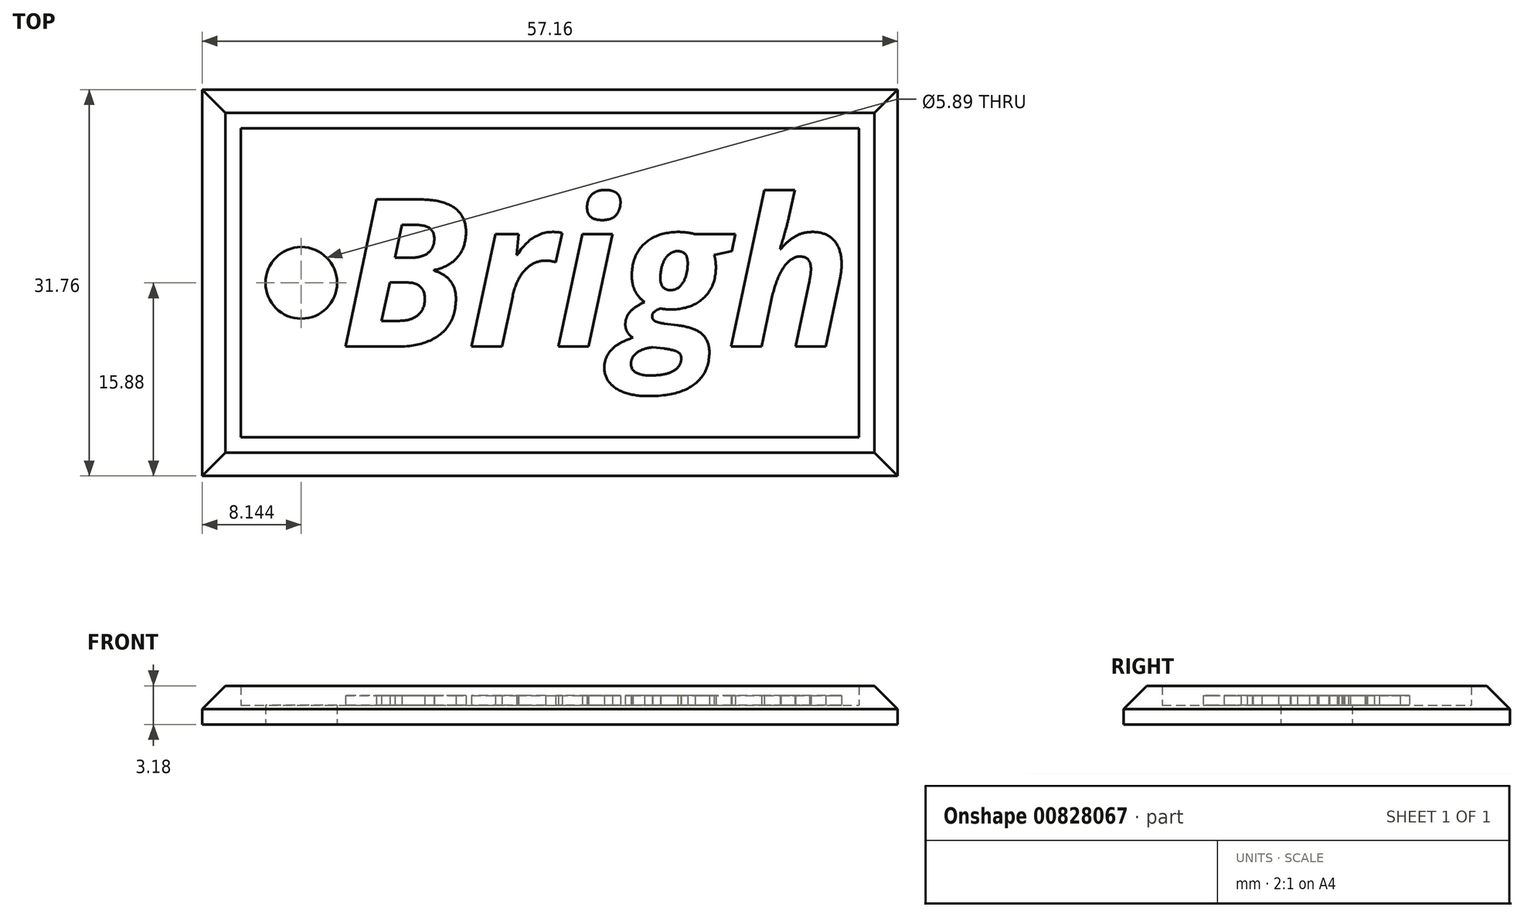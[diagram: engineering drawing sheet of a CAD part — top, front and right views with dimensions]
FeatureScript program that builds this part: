
annotation { "Feature Type Name" : "Feature", "Feature Type Description" : "" }
export const myFeature = defineFeature(function(context is Context, id is Id, definition is map)
    precondition{}
    {
        {
            var Q0;
            Q0=qCreatedBy(makeId("Top.planeOp"),FACE);
            var sketch = newSketch(context, id + "F0", { "sketchPlane" : qUnion([Q0])});
            skLineSegment(sketch, "E0.bottom", {"start": v(0, 0) * mm, "end": v(50.8, 0) * mm});
            skLineSegment(sketch, "E0.top", {"start": v(0, 25.4) * mm, "end": v(50.8, 25.4) * mm});
            skLineSegment(sketch, "E0.left", {"start": v(0, 0) * mm, "end": v(0, 25.4) * mm});
            skLineSegment(sketch, "E0.right", {"start": v(50.8, 0) * mm, "end": v(50.8, 25.4) * mm});
            skCircle(sketch, "E1", {"center": v(4.96, 12.7) * mm, "radius": 2.95 * mm});
            skLineSegment(sketch, "E2.0", {"start": v(-3.18, 28.58) * mm, "end": v(53.98, 28.58) * mm});
            skLineSegment(sketch, "E2.1", {"start": v(-3.18, -3.18) * mm, "end": v(-3.18, 28.58) * mm});
            skLineSegment(sketch, "E2.2", {"start": v(-3.18, -3.18) * mm, "end": v(53.98, -3.18) * mm});
            skLineSegment(sketch, "E2.3", {"start": v(53.98, -3.18) * mm, "end": v(53.98, 28.58) * mm});
            skSolve(sketch);
        }
        {
            var Q0;
            Q0=makeQuery(id+"F0.imprint","IMPRINT",FACE,{"disambiguationData":[TD([[makeQuery(id+"F0.imprint","IMPRINT",EDGE,{"derivedFrom":sQuery(id+"F0.wireOp",EDGE,"E0.bottom")}),1.0]])]});
            extrude(context, id + "F1", {"entities" : qUnion([Q0]), "depth" : 1.59 * mm, "offsetDistance" : 25.4 * mm});
        }
        {
            var Q0;
            Q0 = qSketchRegion(id + "F0", true);
            extrude(context, id + "F2", {"entities" : qUnion([Q0]), "operationType" : NewBodyOperationType.ADD, "depth" : 3.17 * mm, "offsetDistance" : 25.4 * mm});
        }
        {
            var Q0;
            Q0=makeQuery(id+"F2.opExtrude","CAP_EDGE",EDGE,{"disambiguationData":[OSD([sQuery(id+"F0.wireOp",EDGE,"E2.2")])],"isStart":false});
            var Q1;
            Q1=makeQuery(id+"F2.opExtrude","CAP_EDGE",EDGE,{"disambiguationData":[OSD([sQuery(id+"F0.wireOp",EDGE,"E2.1")])],"isStart":false});
            var Q2;
            Q2=makeQuery(id+"F2.opExtrude","CAP_EDGE",EDGE,{"disambiguationData":[OSD([sQuery(id+"F0.wireOp",EDGE,"E2.0")])],"isStart":false});
            var Q3;
            Q3=makeQuery(id+"F2.opExtrude","CAP_EDGE",EDGE,{"disambiguationData":[OSD([sQuery(id+"F0.wireOp",EDGE,"E2.3")])],"isStart":false});
            chamfer(context, id + "F3", {"entities" : qUnion([Q0, Q1, Q2, Q3]), "width" : 1.9 * mm, "tangentPropagation" : true});
        }
        {
            var Q0;
            Q0=makeQuery(id+"F1.opExtrude","CAP_FACE",FACE,{"disambiguationData":[OSD([sQuery(id+"F0.wireOp",EDGE,"E0.bottom"),sQuery(id+"F0.wireOp",EDGE,"E0.top"),sQuery(id+"F0.wireOp",EDGE,"E0.left"),sQuery(id+"F0.wireOp",EDGE,"E0.right"),sQuery(id+"F0.wireOp",EDGE,"E1")])],"isStart":false});
            var sketch = newSketch(context, id + "F4", { "sketchPlane" : qUnion([Q0])});
            skText(sketch, "E3", { "text": "Brigh", "fontName": "OpenSans-BoldItalic.ttf"});
            const initialGuessF4  = {"E3": [0.00815, 0.00746, 1, 0, 0.0122]};
            skSetInitialGuess(sketch, initialGuessF4);
            skSolve(sketch);
        }
        {
            var Q0;
            Q0=makeQuery(id+"F4.imprint","IMPRINT",FACE,{"disambiguationData":[TD([[makeQuery(id+"F4.imprint","IMPRINT",EDGE,{"derivedFrom":sQuery(id+"F4.wireOp",EDGE,"E3.sketch_text.stroke-0")}),1.0]])]});
            var sketch = newSketch(context, id + "F5", { "sketchPlane" : qUnion([Q0])});
            skSolve(sketch);
        }
        {
            var Q0;
            Q0 = qSketchRegion(id + "F5", true);
            var Q1;
            Q1 = qSketchRegion(id + "F4", true);
            extrude(context, id + "F6", {"entities" : qUnion([Q0, Q1]), "operationType" : NewBodyOperationType.ADD, "depth" : 0.8 * mm, "offsetDistance" : 25.4 * mm});
        }
    });
